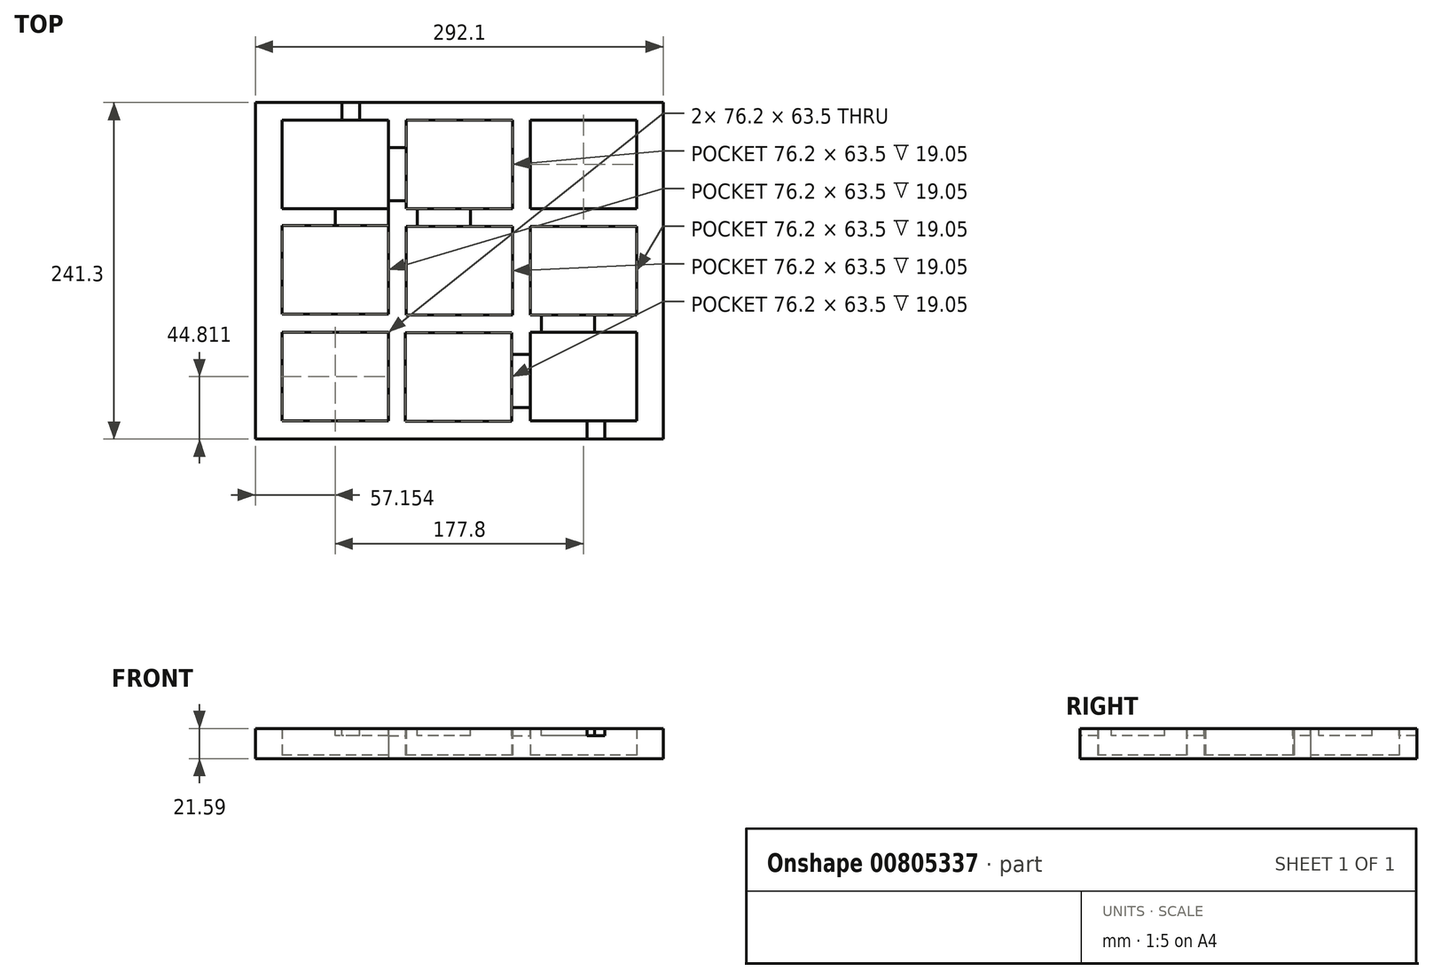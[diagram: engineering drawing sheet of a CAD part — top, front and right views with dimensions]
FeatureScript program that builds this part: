
annotation { "Feature Type Name" : "Feature", "Feature Type Description" : "" }
export const myFeature = defineFeature(function(context is Context, id is Id, definition is map)
    precondition{}
    {
        {
            var Q0;
            Q0=qCreatedBy(makeId("Top.planeOp"),FACE);
            var sketch = newSketch(context, id + "F0", { "sketchPlane" : qUnion([Q0])});
            skLineSegment(sketch, "E0.bottom", {"start": v(141.22, 122.08) * mm, "end": v(-150.88, 122.08) * mm});
            skLineSegment(sketch, "E0.top", {"start": v(141.22, -119.22) * mm, "end": v(-150.88, -119.22) * mm});
            skLineSegment(sketch, "E0.left", {"start": v(141.22, 122.08) * mm, "end": v(141.22, -119.22) * mm});
            skLineSegment(sketch, "E0.right", {"start": v(-150.88, 122.08) * mm, "end": v(-150.88, -119.22) * mm});
            skPoint(sketch, "E0.middle", {"position": v(-4.83, 77.63) * mm});
            skLineSegment(sketch, "E1.bottom", {"start": v(33.27, 109.38) * mm, "end": v(-42.93, 109.38) * mm});
            skLineSegment(sketch, "E1.top", {"start": v(33.27, 45.88) * mm, "end": v(-42.93, 45.88) * mm});
            skLineSegment(sketch, "E1.left", {"start": v(33.27, 109.38) * mm, "end": v(33.27, 45.88) * mm});
            skLineSegment(sketch, "E1.right", {"start": v(-42.93, 109.38) * mm, "end": v(-42.93, 45.88) * mm});
            skPoint(sketch, "E2.middle", {"position": v(-93.73, 2.2) * mm});
            skLineSegment(sketch, "E3.bottom", {"start": v(-55.63, 33.96) * mm, "end": v(-131.83, 33.96) * mm});
            skLineSegment(sketch, "E3.top", {"start": v(-55.63, -29.54) * mm, "end": v(-131.83, -29.54) * mm});
            skLineSegment(sketch, "E3.left", {"start": v(-55.63, 33.96) * mm, "end": v(-55.63, -29.54) * mm});
            skLineSegment(sketch, "E3.right", {"start": v(-131.83, 33.96) * mm, "end": v(-131.83, -29.54) * mm});
            skPoint(sketch, "E4.middle", {"position": v(84.07, 1.43) * mm});
            skLineSegment(sketch, "E5.bottom", {"start": v(122.17, 33.18) * mm, "end": v(45.97, 33.18) * mm});
            skLineSegment(sketch, "E5.top", {"start": v(122.17, -30.32) * mm, "end": v(45.97, -30.32) * mm});
            skLineSegment(sketch, "E5.left", {"start": v(122.17, 33.18) * mm, "end": v(122.17, -30.32) * mm});
            skLineSegment(sketch, "E5.right", {"start": v(45.97, 33.18) * mm, "end": v(45.97, -30.32) * mm});
            skPoint(sketch, "E6.middle", {"position": v(-4.83, 1.43) * mm});
            skLineSegment(sketch, "E7.bottom", {"start": v(33.27, 33.18) * mm, "end": v(-42.93, 33.18) * mm});
            skLineSegment(sketch, "E7.top", {"start": v(33.27, -30.32) * mm, "end": v(-42.93, -30.32) * mm});
            skLineSegment(sketch, "E7.left", {"start": v(33.27, 33.18) * mm, "end": v(33.27, -30.32) * mm});
            skLineSegment(sketch, "E7.right", {"start": v(-42.93, 33.18) * mm, "end": v(-42.93, -30.32) * mm});
            skPoint(sketch, "E8.middle", {"position": v(-5.2, -74.77) * mm});
            skLineSegment(sketch, "E9.bottom", {"start": v(32.9, -43.02) * mm, "end": v(-43.3, -43.02) * mm});
            skLineSegment(sketch, "E9.top", {"start": v(32.9, -106.52) * mm, "end": v(-43.3, -106.52) * mm});
            skLineSegment(sketch, "E9.left", {"start": v(32.9, -43.02) * mm, "end": v(32.9, -106.52) * mm});
            skLineSegment(sketch, "E9.right", {"start": v(-43.3, -43.02) * mm, "end": v(-43.3, -106.52) * mm});
            skLineSegment(sketch, "E10", {"start": v(-55.63, 9.6) * mm, "end": v(-42.93, 9.6) * mm});
            skPoint(sketch, "E11.middle", {"position": v(-93.73, 77.63) * mm});
            skLineSegment(sketch, "E12.bottom", {"start": v(-55.63, 109.38) * mm, "end": v(-131.83, 109.38) * mm});
            skLineSegment(sketch, "E12.top", {"start": v(-55.63, 45.88) * mm, "end": v(-131.83, 45.88) * mm});
            skLineSegment(sketch, "E12.left", {"start": v(-55.63, 109.38) * mm, "end": v(-55.63, 45.88) * mm});
            skLineSegment(sketch, "E12.right", {"start": v(-131.83, 109.38) * mm, "end": v(-131.83, 45.88) * mm});
            skPoint(sketch, "E13.middle", {"position": v(84.07, 77.63) * mm});
            skLineSegment(sketch, "E14.bottom", {"start": v(122.17, 109.38) * mm, "end": v(45.97, 109.38) * mm});
            skLineSegment(sketch, "E14.top", {"start": v(122.17, 45.88) * mm, "end": v(45.97, 45.88) * mm});
            skLineSegment(sketch, "E14.left", {"start": v(122.17, 109.38) * mm, "end": v(122.17, 45.88) * mm});
            skLineSegment(sketch, "E14.right", {"start": v(45.97, 109.38) * mm, "end": v(45.97, 45.88) * mm});
            skPoint(sketch, "E15.middle", {"position": v(84.07, -74.4) * mm});
            skLineSegment(sketch, "E16.bottom", {"start": v(122.17, -42.66) * mm, "end": v(45.97, -42.66) * mm});
            skLineSegment(sketch, "E16.top", {"start": v(122.17, -106.16) * mm, "end": v(45.97, -106.16) * mm});
            skLineSegment(sketch, "E16.left", {"start": v(122.17, -42.66) * mm, "end": v(122.17, -106.16) * mm});
            skLineSegment(sketch, "E16.right", {"start": v(45.97, -42.66) * mm, "end": v(45.97, -106.16) * mm});
            skPoint(sketch, "E17.middle", {"position": v(-93.73, -74.4) * mm});
            skLineSegment(sketch, "E18.bottom", {"start": v(-55.63, -42.66) * mm, "end": v(-131.83, -42.66) * mm});
            skLineSegment(sketch, "E18.top", {"start": v(-55.63, -106.16) * mm, "end": v(-131.83, -106.16) * mm});
            skLineSegment(sketch, "E18.left", {"start": v(-55.63, -42.66) * mm, "end": v(-55.63, -106.16) * mm});
            skLineSegment(sketch, "E18.right", {"start": v(-131.83, -42.66) * mm, "end": v(-131.83, -106.16) * mm});
            skSolve(sketch);
        }
        {
            var Q0;
            Q0=makeQuery(id+"F0.imprint","IMPRINT",FACE,{"disambiguationData":[TD([[makeQuery(id+"F0.imprint","IMPRINT",EDGE,{"derivedFrom":sQuery(id+"F0.wireOp",EDGE,"E0.bottom")}),1.0]])]});
            extrude(context, id + "F1", {"entities" : qUnion([Q0]), "depth" : 21.59 * mm, "offsetDistance" : 25.4 * mm});
        }
        {
            var Q0;
            Q0=makeQuery(id+"F0.imprint","IMPRINT",FACE,{"disambiguationData":[TD([[makeQuery(id+"F0.imprint","IMPRINT",EDGE,{"derivedFrom":sQuery(id+"F0.wireOp",EDGE,"E1.bottom")}),1.0]])]});
            var Q1;
            {var subQ1=sQuery(id+"F0.wireOp",EDGE,"E7.bottom");Q1=makeQuery(id+"F0.imprint","IMPRINT",FACE,{"disambiguationData":[TD([[makeQuery(id+"F0.imprint","IMPRINT",EDGE,{"derivedFrom":subQ1}),1.0]])]});}
            var Q2;
            Q2=makeQuery(id+"F0.imprint","IMPRINT",FACE,{"disambiguationData":[TD([[makeQuery(id+"F0.imprint","IMPRINT",EDGE,{"derivedFrom":sQuery(id+"F0.wireOp",EDGE,"E9.bottom")}),1.0]])]});
            var Q3;
            {var subQ3=sQuery(id+"F0.wireOp",EDGE,"E3.bottom");Q3=makeQuery(id+"F0.imprint","IMPRINT",FACE,{"disambiguationData":[TD([[makeQuery(id+"F0.imprint","IMPRINT",EDGE,{"derivedFrom":subQ3}),1.0]])]});}
            var Q4;
            Q4=makeQuery(id+"F0.imprint","IMPRINT",FACE,{"disambiguationData":[TD([[makeQuery(id+"F0.imprint","IMPRINT",EDGE,{"derivedFrom":sQuery(id+"F0.wireOp",EDGE,"E5.bottom")}),1.0]])]});
            extrude(context, id + "F2", {"entities" : qUnion([Q0, Q1, Q2, Q3, Q4]), "operationType" : NewBodyOperationType.ADD, "depth" : 2.54 * mm, "offsetDistance" : 25.4 * mm});
        }
        {
            var Q0;
            Q0=makeQuery(id+"F1.opExtrude","CAP_FACE",FACE,{"disambiguationData":[OSD([sQuery(id+"F0.wireOp",EDGE,"E0.bottom"),sQuery(id+"F0.wireOp",EDGE,"E0.top"),sQuery(id+"F0.wireOp",EDGE,"E0.left"),sQuery(id+"F0.wireOp",EDGE,"E0.right"),sQuery(id+"F0.wireOp",EDGE,"E1.bottom"),sQuery(id+"F0.wireOp",EDGE,"E1.top"),sQuery(id+"F0.wireOp",EDGE,"E1.left"),sQuery(id+"F0.wireOp",EDGE,"E1.right"),sQuery(id+"F0.wireOp",EDGE,"E3.bottom"),sQuery(id+"F0.wireOp",EDGE,"E3.top"),sQuery(id+"F0.wireOp",EDGE,"E3.left"),sQuery(id+"F0.wireOp",EDGE,"E3.right"),sQuery(id+"F0.wireOp",EDGE,"E5.bottom"),sQuery(id+"F0.wireOp",EDGE,"E5.top"),sQuery(id+"F0.wireOp",EDGE,"E5.left"),sQuery(id+"F0.wireOp",EDGE,"E5.right"),sQuery(id+"F0.wireOp",EDGE,"E7.bottom"),sQuery(id+"F0.wireOp",EDGE,"E7.top"),sQuery(id+"F0.wireOp",EDGE,"E7.left"),sQuery(id+"F0.wireOp",EDGE,"E7.right"),sQuery(id+"F0.wireOp",EDGE,"E9.bottom"),sQuery(id+"F0.wireOp",EDGE,"E9.top"),sQuery(id+"F0.wireOp",EDGE,"E9.left"),sQuery(id+"F0.wireOp",EDGE,"E9.right"),sQuery(id+"F0.wireOp",EDGE,"E12.bottom"),sQuery(id+"F0.wireOp",EDGE,"E12.top"),sQuery(id+"F0.wireOp",EDGE,"E12.left"),sQuery(id+"F0.wireOp",EDGE,"E12.right"),sQuery(id+"F0.wireOp",EDGE,"E14.bottom"),sQuery(id+"F0.wireOp",EDGE,"E14.top"),sQuery(id+"F0.wireOp",EDGE,"E14.left"),sQuery(id+"F0.wireOp",EDGE,"E14.right"),sQuery(id+"F0.wireOp",EDGE,"E16.bottom"),sQuery(id+"F0.wireOp",EDGE,"E16.top"),sQuery(id+"F0.wireOp",EDGE,"E16.left"),sQuery(id+"F0.wireOp",EDGE,"E16.right"),sQuery(id+"F0.wireOp",EDGE,"E18.bottom"),sQuery(id+"F0.wireOp",EDGE,"E18.top"),sQuery(id+"F0.wireOp",EDGE,"E18.left"),sQuery(id+"F0.wireOp",EDGE,"E18.right")])],"isStart":false});
            var sketch = newSketch(context, id + "F3", { "sketchPlane" : qUnion([Q0])});
            skLineSegment(sketch, "E19.bottom", {"start": v(-93.69, 45.88) * mm, "end": v(-55.59, 45.88) * mm});
            skLineSegment(sketch, "E19.top", {"start": v(-93.69, 33.96) * mm, "end": v(-55.59, 33.96) * mm});
            skLineSegment(sketch, "E19.left", {"start": v(-93.69, 45.88) * mm, "end": v(-93.69, 33.96) * mm});
            skLineSegment(sketch, "E19.right", {"start": v(-55.59, 45.88) * mm, "end": v(-55.59, 33.96) * mm});
            skLineSegment(sketch, "E20.bottom", {"start": v(-55.63, 89.88) * mm, "end": v(-42.93, 89.88) * mm});
            skLineSegment(sketch, "E20.top", {"start": v(-55.63, 51.78) * mm, "end": v(-42.93, 51.78) * mm});
            skLineSegment(sketch, "E20.left", {"start": v(-55.63, 89.88) * mm, "end": v(-55.63, 51.78) * mm});
            skLineSegment(sketch, "E20.right", {"start": v(-42.93, 89.88) * mm, "end": v(-42.93, 51.78) * mm});
            skLineSegment(sketch, "E21.bottom", {"start": v(-34.82, 45.88) * mm, "end": v(3.28, 45.88) * mm});
            skLineSegment(sketch, "E21.top", {"start": v(-34.82, 33.18) * mm, "end": v(3.28, 33.18) * mm});
            skLineSegment(sketch, "E21.left", {"start": v(-34.82, 45.88) * mm, "end": v(-34.82, 33.18) * mm});
            skLineSegment(sketch, "E21.right", {"start": v(3.28, 45.88) * mm, "end": v(3.28, 33.18) * mm});
            skLineSegment(sketch, "E22.bottom", {"start": v(-88.7, 122.08) * mm, "end": v(-76, 122.08) * mm});
            skLineSegment(sketch, "E22.top", {"start": v(-88.7, 109.38) * mm, "end": v(-76, 109.38) * mm});
            skLineSegment(sketch, "E22.left", {"start": v(-88.7, 122.08) * mm, "end": v(-88.7, 109.38) * mm});
            skLineSegment(sketch, "E22.right", {"start": v(-76, 122.08) * mm, "end": v(-76, 109.38) * mm});
            skLineSegment(sketch, "E23.bottom", {"start": v(86.61, -106.16) * mm, "end": v(99.31, -106.16) * mm});
            skLineSegment(sketch, "E23.top", {"start": v(86.61, -119.22) * mm, "end": v(99.31, -119.22) * mm});
            skLineSegment(sketch, "E23.left", {"start": v(86.61, -106.16) * mm, "end": v(86.61, -119.22) * mm});
            skLineSegment(sketch, "E23.right", {"start": v(99.31, -106.16) * mm, "end": v(99.31, -119.22) * mm});
            skLineSegment(sketch, "E24.bottom", {"start": v(54.14, -30.32) * mm, "end": v(92.24, -30.32) * mm});
            skLineSegment(sketch, "E24.top", {"start": v(54.14, -42.66) * mm, "end": v(92.24, -42.66) * mm});
            skLineSegment(sketch, "E24.left", {"start": v(54.14, -30.32) * mm, "end": v(54.14, -42.66) * mm});
            skLineSegment(sketch, "E24.right", {"start": v(92.24, -30.32) * mm, "end": v(92.24, -42.66) * mm});
            skLineSegment(sketch, "E25.bottom", {"start": v(32.9, -58.65) * mm, "end": v(45.97, -58.65) * mm});
            skLineSegment(sketch, "E25.top", {"start": v(32.9, -96.75) * mm, "end": v(45.97, -96.75) * mm});
            skLineSegment(sketch, "E25.left", {"start": v(32.9, -58.65) * mm, "end": v(32.9, -96.75) * mm});
            skLineSegment(sketch, "E25.right", {"start": v(45.97, -58.65) * mm, "end": v(45.97, -96.75) * mm});
            skSolve(sketch);
        }
        {
            var Q0;
            Q0 = qSketchRegion(id + "F3", true);
            extrude(context, id + "F4", {"entities" : qUnion([Q0]), "operationType" : NewBodyOperationType.REMOVE, "oppositeDirection" : true, "depth" : 5.08 * mm, "offsetDistance" : 25.4 * mm});
        }
    });
